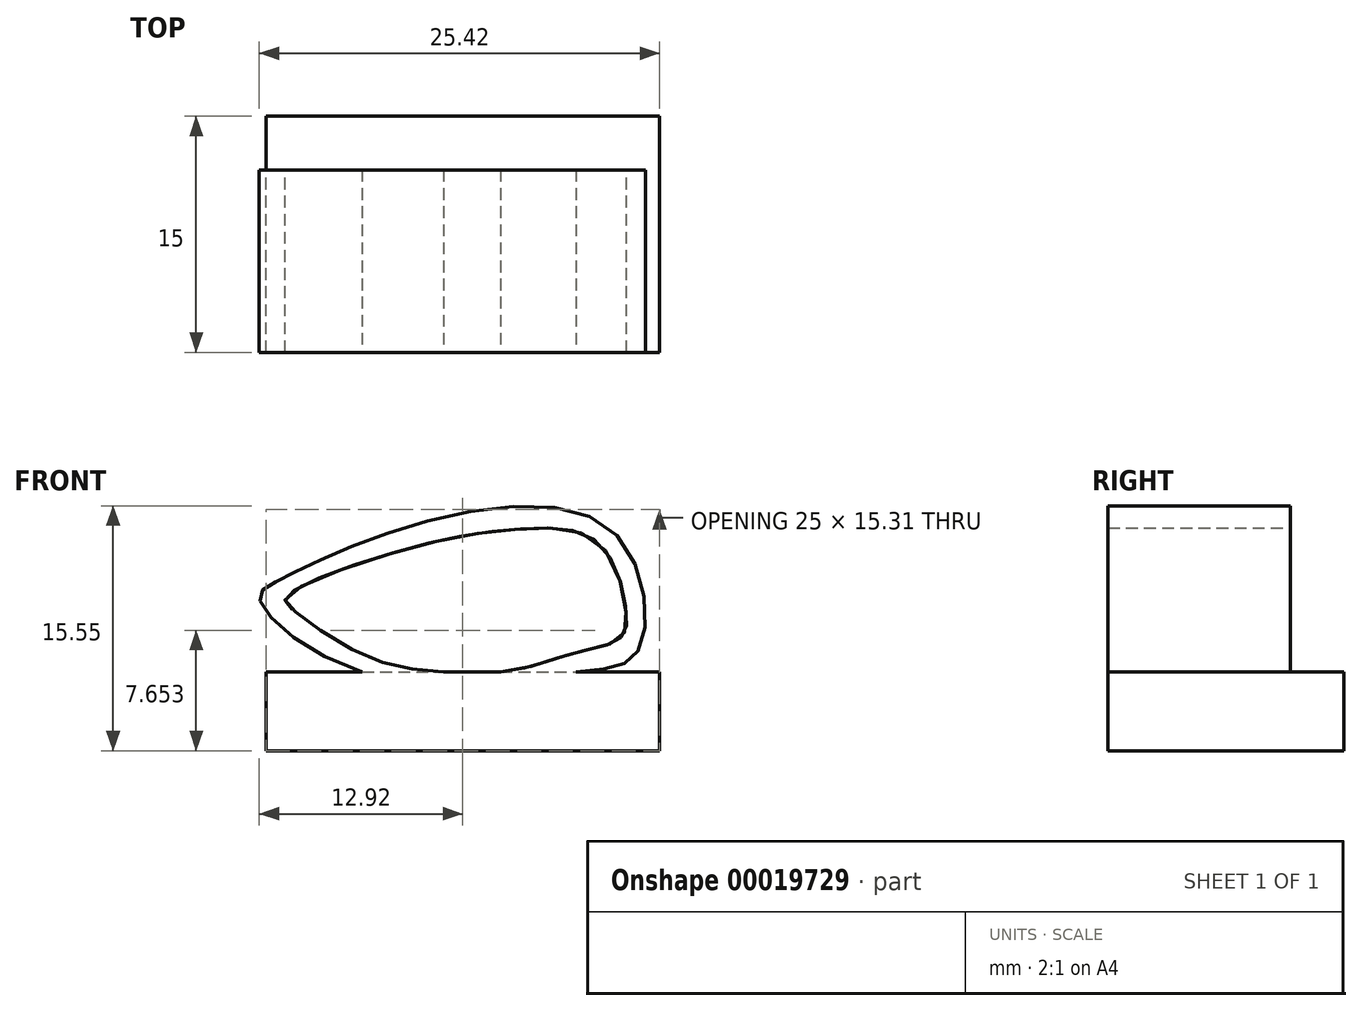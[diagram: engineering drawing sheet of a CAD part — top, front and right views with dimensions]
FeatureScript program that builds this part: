
annotation { "Feature Type Name" : "Feature", "Feature Type Description" : "" }
export const myFeature = defineFeature(function(context is Context, id is Id, definition is map)
    precondition{}
    {
        {
            var Q0;
            Q0=qCreatedBy(makeId("Top.planeOp"),FACE);
            var sketch = newSketch(context, id + "F0", { "sketchPlane" : qUnion([Q0])});
            skLineSegment(sketch, "E0.bottom", {"start": v(0, 0) * mm, "end": v(-25, 0) * mm});
            skLineSegment(sketch, "E0.top", {"start": v(0, 15) * mm, "end": v(-25, 15) * mm});
            skLineSegment(sketch, "E0.left", {"start": v(0, 0) * mm, "end": v(0, 15) * mm});
            skLineSegment(sketch, "E0.right", {"start": v(-25, 0) * mm, "end": v(-25, 15) * mm});
            skSolve(sketch);
        }
        {
            var Q0;
            Q0=makeQuery(id+"F0.imprint","IMPRINT",FACE,{"disambiguationData":[TD([[makeQuery(id+"F0.imprint","IMPRINT",EDGE,{"derivedFrom":sQuery(id+"F0.wireOp",EDGE,"E0.bottom")}),-1.0]])]});
            extrude(context, id + "F1", {"entities" : qUnion([Q0]), "depth" : 5 * mm});
        }
        {
            var Q0;
            Q0=qCreatedBy(makeId("Front.planeOp"),FACE);
            var sketch = newSketch(context, id + "F2", { "sketchPlane" : qUnion([Q0])});
            skFitSpline(sketch, "E1", {"points": [v(-18.9, 5) * mm, v(-25.42, 9.7) * mm, v(-24.43, 10.68) * mm, v(-16.54, 14.06) * mm, v(-3.05, 14.02) * mm, v(-1.3, 6.47) * mm, v(-4.96, 5.04) * mm, v(-18.9, 5) * mm]});
            skSolve(sketch);
        }
        {
            var Q0;
            Q0=makeQuery(id+"F2.imprint","IMPRINT",FACE,{"disambiguationData":[TD([[makeQuery(id+"F2.imprint","IMPRINT",EDGE,{"derivedFrom":sQuery(id+"F2.wireOp",EDGE,"E1")}),-1.0]])]});
            var sketch = newSketch(context, id + "F3", { "sketchPlane" : qUnion([Q0])});
            skFitSpline(sketch, "E2", {"points": [v(-5.42, 6.21) * mm, v(-2.58, 7.09) * mm, v(-2.1, 8.65) * mm, v(-3.8, 13.1) * mm, v(-8.32, 14.12) * mm, v(-16.23, 12.77) * mm, v(-23.74, 9.73) * mm, v(-23.33, 8.98) * mm, v(-18.94, 6.14) * mm, v(-14.48, 5.06) * mm, v(-9.13, 5.13) * mm, v(-5.42, 6.21) * mm]});
            skSolve(sketch);
        }
        {
            var Q0;
            Q0=makeQuery(id+"F3.imprint","IMPRINT",FACE,{"disambiguationData":[TD([[makeQuery(id+"F3.imprint","IMPRINT",EDGE,{"derivedFrom":sQuery(id+"F3.wireOp",EDGE,"E2")}),-1.0]])]});
            extrude(context, id + "F4", {"entities" : qUnion([Q0]), "operationType" : NewBodyOperationType.ADD, "oppositeDirection" : true, "depth" : 11.58 * mm});
        }
        {
            var Q0;
            Q0=makeQuery(id+"F1.opExtrude","SWEPT_BODY",BODY,{"disambiguationData":[OSD([sQuery(id+"F0.wireOp",EDGE,"E0.bottom"),sQuery(id+"F0.wireOp",EDGE,"E0.top"),sQuery(id+"F0.wireOp",EDGE,"E0.left"),sQuery(id+"F0.wireOp",EDGE,"E0.right")])]});
            transform(context, id + "F5", {"entities" : qUnion([Q0]), "transformType" : TransformType.TRANSLATION_3D, "dx" : 0 * mm, "dy" : 0 * mm, "dz" : 0 * mm, "makeCopy" : true});
        }
    });
